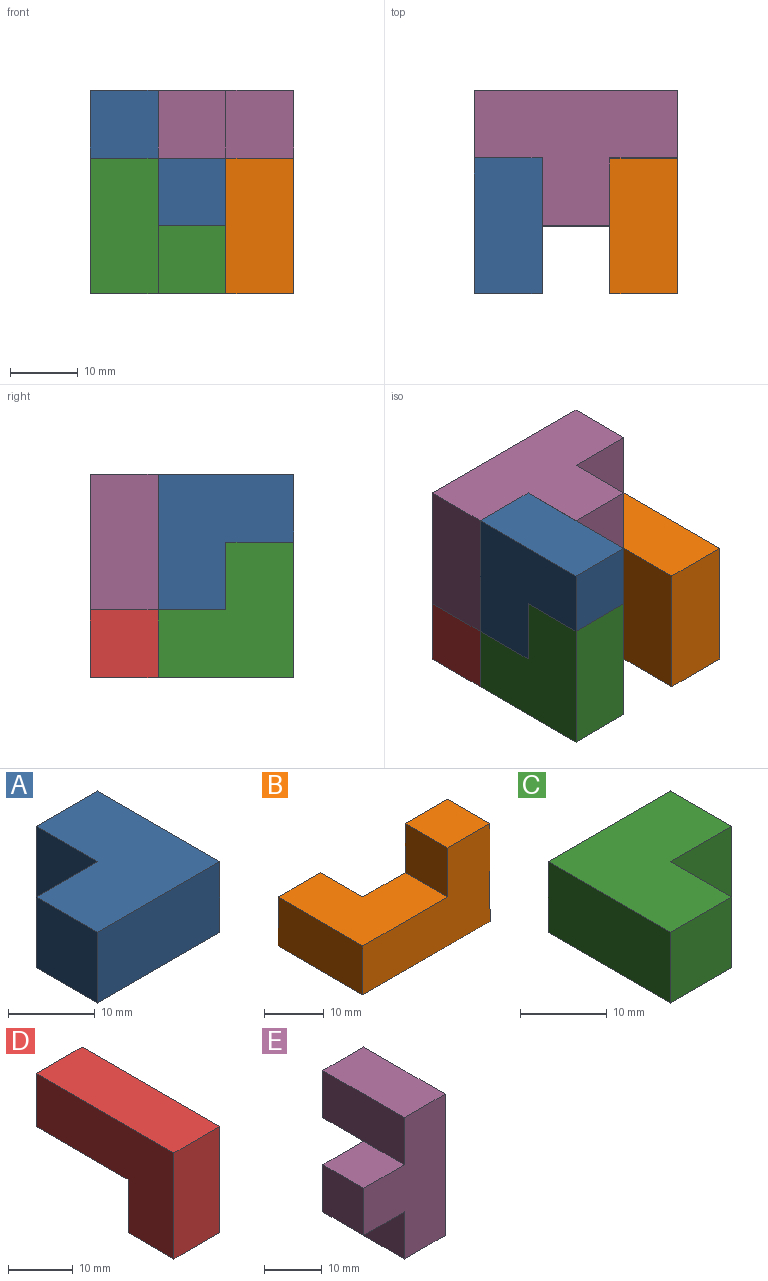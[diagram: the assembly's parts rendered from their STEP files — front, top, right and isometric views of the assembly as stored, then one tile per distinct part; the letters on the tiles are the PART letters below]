
ASSEMBLY  parts=5 mates=3
PART A: 10 faces, bbox 20x20x20 mm
  f0: plane 10x10mm, normal (-1,0,0), area 100mm2, adj f1,f6,f7,f8
  f1: plane 20x10mm, normal (0,-1,0), area 200mm2, adj f0,f3,f7,f8
  f2: plane 10x10mm, normal (0,0,-1), area 100mm2, adj f3,f4,f5,f9
  f3: plane 20x20mm, normal (1,0,0), area 300mm2, adj f1,f2,f4,f7,f8,f9
  f4: plane 20x10mm, normal (0,1,0), area 200mm2, adj f2,f3,f5,f7
  f5: plane 20x10mm, normal (-1,0,0), area 200mm2, adj f2,f4,f6,f7,f9
  f6: plane 10x10mm, normal (0,1,0), area 100mm2, adj f0,f5,f7,f8
  f7: plane 20x20mm, normal (0,0,1), area 300mm2, adj f0,f1,f3,f4,f5,f6
  f8: plane 20x10mm, normal (0,0,-1), area 200mm2, adj f0,f1,f3,f6,f9
  f9: plane 10x10mm, normal (0,-1,0), area 100mm2, adj f2,f3,f5,f8
PART B: 10 faces, bbox 30x20x20 mm
  f0: plane 20x20mm, normal (0,0,1), area 300mm2, adj f4,f5,f6,f7,f8,f9
  f1: plane 30x20mm, normal (0,0,-1), area 400mm2, adj f2,f5,f6,f7,f8,f9
  f2: plane 20x10mm, normal (1,0,0), area 200mm2, adj f1,f3,f7,f8
  f3: plane 10x10mm, normal (0,0,1), area 100mm2, adj f2,f4,f7,f8
  f4: plane 10x10mm, normal (-1,0,0), area 100mm2, adj f0,f3,f7,f8
  f5: plane 20x10mm, normal (-1,0,0), area 200mm2, adj f0,f1,f6,f7
  f6: plane 10x10mm, normal (0,1,0), area 100mm2, adj f0,f1,f5,f9
  f7: plane 30x20mm, normal (0,-1,0), area 400mm2, adj f0,f1,f2,f3,f4,f5
  f8: plane 20x20mm, normal (0,1,0), area 300mm2, adj f0,f1,f2,f3,f4,f9
  f9: plane 10x10mm, normal (1,0,0), area 100mm2, adj f0,f1,f6,f8
PART C: 10 faces, bbox 20x20x20 mm
  f0: plane 20x20mm, normal (0,0,1), area 300mm2, adj f3,f4,f6,f7,f8,f9
  f1: plane 10x10mm, normal (-1,0,0), area 100mm2, adj f2,f5,f7,f9
  f2: plane 10x10mm, normal (0,0,-1), area 100mm2, adj f1,f6,f7,f9
  f3: plane 10x10mm, normal (0,-1,0), area 100mm2, adj f0,f4,f5,f8
  f4: plane 20x10mm, normal (-1,0,0), area 200mm2, adj f0,f3,f5,f7
  f5: plane 20x10mm, normal (0,0,-1), area 200mm2, adj f1,f3,f4,f7,f8
  f6: plane 20x10mm, normal (1,0,0), area 200mm2, adj f0,f2,f7,f9
  f7: plane 20x20mm, normal (0,1,0), area 300mm2, adj f0,f1,f2,f4,f5,f6
  f8: plane 10x10mm, normal (1,0,0), area 100mm2, adj f0,f3,f5,f9
  f9: plane 20x10mm, normal (0,-1,0), area 200mm2, adj f0,f1,f2,f6,f8
PART D: 8 faces, bbox 10x30x20 mm
  f0: plane 30x20mm, normal (-1,0,0), area 400mm2, adj f1,f3,f4,f5,f6,f7
  f1: plane 10x10mm, normal (0,0,-1), area 100mm2, adj f0,f2,f5,f7
  f2: plane 30x20mm, normal (1,0,0), area 400mm2, adj f1,f3,f4,f5,f6,f7
  f3: plane 30x10mm, normal (0,0,1), area 300mm2, adj f0,f2,f4,f5
  f4: plane 10x10mm, normal (0,1,0), area 100mm2, adj f0,f2,f3,f6
  f5: plane 20x10mm, normal (0,-1,0), area 200mm2, adj f0,f1,f2,f3
  f6: plane 20x10mm, normal (0,0,-1), area 200mm2, adj f0,f2,f4,f7
  f7: plane 10x10mm, normal (0,1,0), area 100mm2, adj f0,f1,f2,f6
PART E: 12 faces, bbox 20x20x30 mm
  f0: plane 30x20mm, normal (0,-1,0), area 400mm2, adj f2,f3,f4,f6,f7,f8,f10,f11
  f1: plane 20x20mm, normal (0,1,0), area 300mm2, adj f3,f4,f6,f7,f8,f9,f11
  f2: plane 20x10mm, normal (0,0,1), area 200mm2, adj f0,f5,f8,f10
  f3: plane 10x10mm, normal (-1,0,0), area 100mm2, adj f0,f1,f6,f11
  f4: plane 10x10mm, normal (0,0,-1), area 100mm2, adj f0,f1,f7,f8
  f5: plane 10x10mm, normal (0,1,0), area 100mm2, adj f2,f8,f9,f10
  f6: plane 10x10mm, normal (0,0,-1), area 100mm2, adj f0,f1,f3,f7
  f7: plane 10x10mm, normal (-1,0,0), area 100mm2, adj f0,f1,f4,f6
  f8: plane 30x20mm, normal (1,0,0), area 400mm2, adj f0,f1,f2,f4,f5,f9
  f9: plane 10x10mm, normal (0,0,-1), area 100mm2, adj f1,f5,f8,f10
  f10: plane 20x10mm, normal (-1,0,0), area 200mm2, adj f0,f2,f5,f9,f11
  f11: plane 10x10mm, normal (0,0,1), area 100mm2, adj f0,f1,f3,f10
PLACE A rot(axis=(-0.58,-0.58,0.58),120deg) t=(-46.36,5.47,-46.86)mm
PLACE B rot(axis=(-0.58,-0.58,0.58),120deg) t=(-42.34,0.2,-28.14)mm
PLACE C rot(axis=(-0.58,-0.58,0.58),120deg) t=(-17.07,11.76,-48.14)mm
PLACE D rot(axis=(-0.58,0.58,0.58),120deg) t=(-16.36,28.88,-55.76)mm
PLACE E rot(axis=(-0.58,-0.58,0.58),120deg) t=(-26.36,22.51,-18.14)mm
MATE fastened C.f3 <-> A.f6  axis (0,0,1) through (-41.36,-9.53,-28.14)mm
MATE fastened A.f2 <-> B.f0  axis (1,0,0) through (-26.36,5.47,-33.14)mm
MATE fastened D.f0 <-> E.f5  axis (0,0,1) through (-46.36,10.47,-38.14)mm
